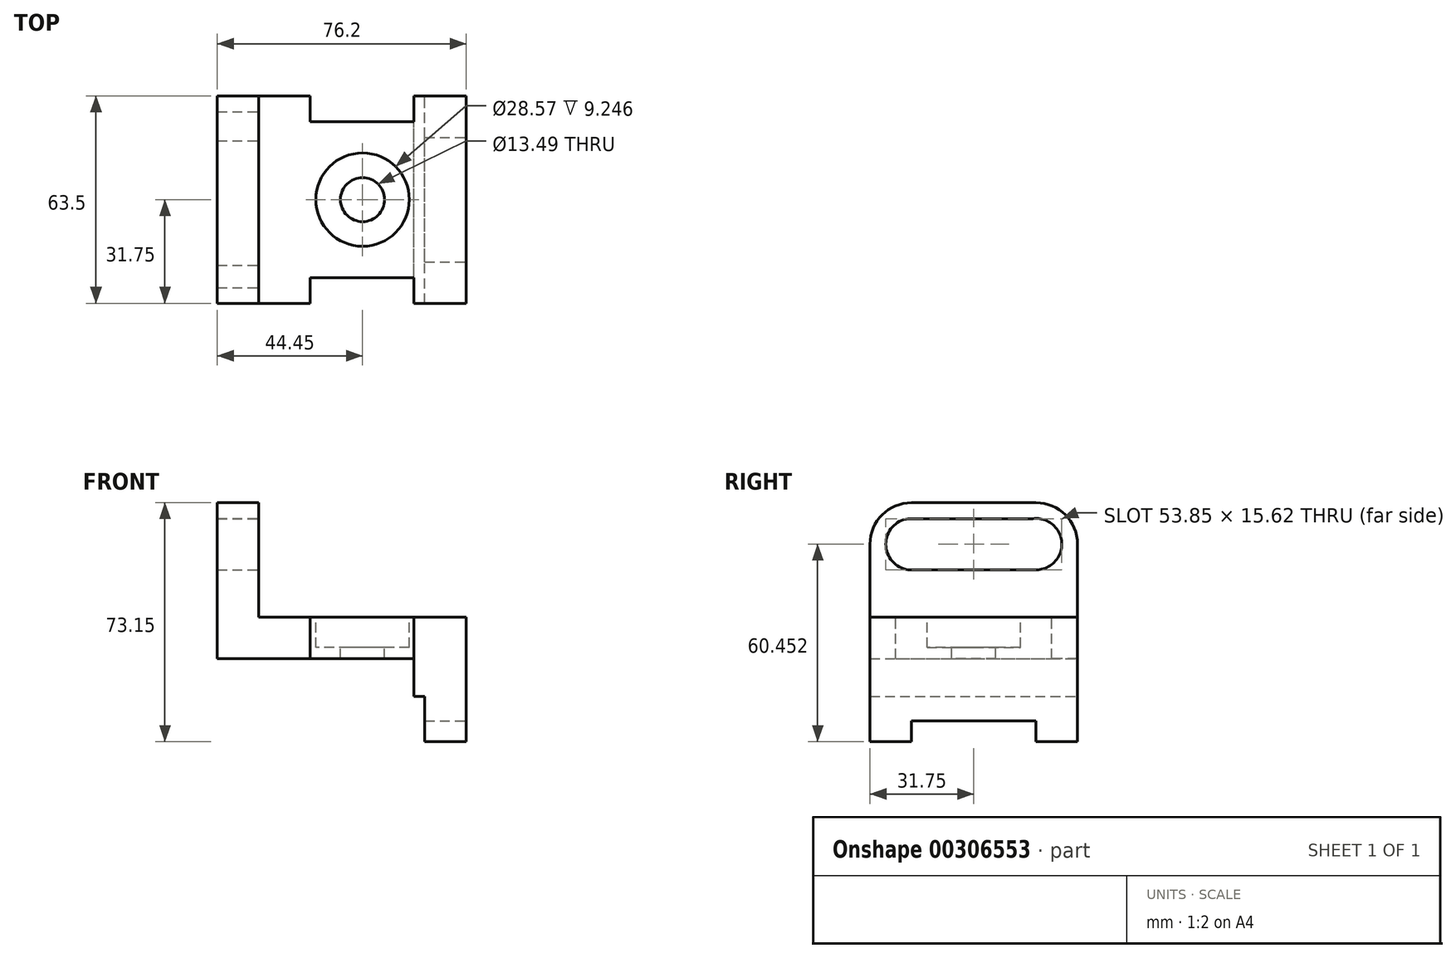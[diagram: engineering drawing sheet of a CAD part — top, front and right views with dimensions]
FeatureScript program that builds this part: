
annotation { "Feature Type Name" : "Feature", "Feature Type Description" : "" }
export const myFeature = defineFeature(function(context is Context, id is Id, definition is map)
    precondition{}
    {
        {
            var Q0;
            Q0=qCreatedBy(makeId("Front.planeOp"),FACE);
            var sketch = newSketch(context, id + "F0", { "sketchPlane" : qUnion([Q0])});
            skLineSegment(sketch, "E0", {"start": v(0, 0) * mm, "end": v(47.5, 0) * mm});
            skLineSegment(sketch, "E1", {"start": v(47.5, 0) * mm, "end": v(47.5, -11.58) * mm});
            skLineSegment(sketch, "E2", {"start": v(47.5, -11.58) * mm, "end": v(50.8, -11.58) * mm});
            skLineSegment(sketch, "E3", {"start": v(50.8, -11.58) * mm, "end": v(50.8, -25.4) * mm});
            skLineSegment(sketch, "E4", {"start": v(50.8, -25.4) * mm, "end": v(63.5, -25.4) * mm});
            skLineSegment(sketch, "E5", {"start": v(63.5, -25.4) * mm, "end": v(63.5, 12.7) * mm});
            skLineSegment(sketch, "E6", {"start": v(63.5, 12.7) * mm, "end": v(0, 12.7) * mm});
            skLineSegment(sketch, "E7", {"start": v(0, 12.7) * mm, "end": v(0, 0) * mm});
            skLineSegment(sketch, "E8", {"start": v(47.5, -11.58) * mm, "end": v(47.5, 0) * mm});
            skLineSegment(sketch, "E9", {"start": v(47.5, 12.7) * mm, "end": v(63.5, 12.7) * mm});
            skPoint(sketch, "E10.start.orphan", {"position": v(7.87, 0) * mm});
            skSolve(sketch);
        }
        {
            var Q0;
            Q0=makeQuery(id+"F0.imprint","IMPRINT",FACE,{"disambiguationData":[TD([[makeQuery(id+"F0.imprint","IMPRINT",EDGE,{"derivedFrom":sQuery(id+"F0.wireOp",EDGE,"E0")}),1.0]])]});
            extrude(context, id + "F1", {"entities" : qUnion([Q0]), "depth" : 63.5 * mm});
        }
        {
            var Q0;
            Q0=makeQuery(id+"F1.opExtrude","SWEPT_FACE",FACE,{"disambiguationData":[OSD([sQuery(id+"F0.wireOp",EDGE,"E5")])]});
            var sketch = newSketch(context, id + "F2", { "sketchPlane" : qUnion([Q0])});
            skLineSegment(sketch, "E11", {"start": v(-50.8, -25.4) * mm, "end": v(-50.8, -19.05) * mm});
            skLineSegment(sketch, "E12", {"start": v(-50.8, -19.05) * mm, "end": v(-12.7, -19.05) * mm});
            skLineSegment(sketch, "E13", {"start": v(-12.7, -19.05) * mm, "end": v(-12.7, -25.4) * mm});
            skLineSegment(sketch, "E14", {"start": v(-50.8, -25.4) * mm, "end": v(-63.5, -25.4) * mm});
            skLineSegment(sketch, "E15", {"start": v(-63.5, -25.4) * mm, "end": v(-63.5, 12.7) * mm});
            skLineSegment(sketch, "E16", {"start": v(-63.5, 12.7) * mm, "end": v(0, 12.7) * mm});
            skLineSegment(sketch, "E17", {"start": v(0, 12.7) * mm, "end": v(0, -25.4) * mm});
            skLineSegment(sketch, "E18", {"start": v(0, -25.4) * mm, "end": v(-12.7, -25.4) * mm});
            skLineSegment(sketch, "E19", {"start": v(-63.5, -25.4) * mm, "end": v(0, -25.4) * mm});
            skSolve(sketch);
        }
        {
            var Q0;
            {var subQ0=sQuery(id+"F2.wireOp",EDGE,"E11");Q0=makeQuery(id+"F2.imprint","IMPRINT",FACE,{"disambiguationData":[TD([[makeQuery(id+"F2.imprint","IMPRINT",EDGE,{"derivedFrom":subQ0}),-1.0]])]});}
            extrude(context, id + "F3", {"entities" : qUnion([Q0]), "operationType" : NewBodyOperationType.REMOVE, "endBound" : BoundingType.THROUGH_ALL, "oppositeDirection" : true, "depth" : 25.4 * mm});
        }
        {
            var Q0;
            Q0=makeQuery(id+"F1.opExtrude","SWEPT_FACE",FACE,{"disambiguationData":[OSD([sQuery(id+"F0.wireOp",EDGE,"E6"),sQuery(id+"F0.wireOp",EDGE,"E9")])]});
            var sketch = newSketch(context, id + "F4", { "sketchPlane" : qUnion([Q0])});
            skLineSegment(sketch, "E20", {"start": v(15.75, -63.5) * mm, "end": v(15.75, -55.63) * mm});
            skLineSegment(sketch, "E21", {"start": v(15.75, -55.63) * mm, "end": v(47.5, -55.63) * mm});
            skLineSegment(sketch, "E22", {"start": v(47.5, -55.63) * mm, "end": v(47.5, -63.5) * mm});
            skLineSegment(sketch, "E23", {"start": v(15.75, 0) * mm, "end": v(15.75, -7.87) * mm});
            skLineSegment(sketch, "E24", {"start": v(15.75, -7.87) * mm, "end": v(47.5, -7.87) * mm});
            skLineSegment(sketch, "E25", {"start": v(47.5, -7.87) * mm, "end": v(47.5, 0) * mm});
            skLineSegment(sketch, "E26", {"start": v(47.5, 0) * mm, "end": v(15.75, 0) * mm});
            skLineSegment(sketch, "E27", {"start": v(15.75, -63.5) * mm, "end": v(47.5, -63.5) * mm});
            skCircle(sketch, "E28", {"center": v(31.75, -31.75) * mm, "radius": 14.29 * mm});
            skCircle(sketch, "E29", {"center": v(31.75, -31.75) * mm, "radius": 6.74 * mm});
            skSolve(sketch);
        }
        {
            var Q0;
            Q0=makeQuery(id+"F4.imprint","IMPRINT",FACE,{"disambiguationData":[TD([[makeQuery(id+"F4.imprint","IMPRINT",EDGE,{"derivedFrom":sQuery(id+"F4.wireOp",EDGE,"E23")}),1.0]])]});
            var Q1;
            Q1=makeQuery(id+"F4.imprint","IMPRINT",FACE,{"disambiguationData":[TD([[makeQuery(id+"F4.imprint","IMPRINT",EDGE,{"derivedFrom":sQuery(id+"F4.wireOp",EDGE,"E20")}),-1.0]])]});
            extrude(context, id + "F5", {"entities" : qUnion([Q0, Q1]), "operationType" : NewBodyOperationType.REMOVE, "endBound" : BoundingType.THROUGH_ALL, "oppositeDirection" : true, "depth" : 25.4 * mm});
        }
        {
            var Q0;
            Q0=makeQuery(id+"F4.imprint","IMPRINT",FACE,{"disambiguationData":[TD([[makeQuery(id+"F4.imprint","IMPRINT",EDGE,{"derivedFrom":sQuery(id+"F4.wireOp",EDGE,"E28")}),1.0]])]});
            extrude(context, id + "F6", {"entities" : qUnion([Q0]), "operationType" : NewBodyOperationType.REMOVE, "oppositeDirection" : true, "depth" : 9.25 * mm});
        }
        {
            var Q0;
            Q0=makeQuery(id+"F4.imprint","IMPRINT",FACE,{"disambiguationData":[TD([[makeQuery(id+"F4.imprint","IMPRINT",EDGE,{"derivedFrom":sQuery(id+"F4.wireOp",EDGE,"E29")}),1.0]])]});
            extrude(context, id + "F7", {"entities" : qUnion([Q0]), "operationType" : NewBodyOperationType.REMOVE, "endBound" : BoundingType.THROUGH_ALL, "oppositeDirection" : true, "depth" : 25.4 * mm});
        }
        {
            var Q0;
            Q0=makeQuery(id+"F1.opExtrude","SWEPT_FACE",FACE,{"disambiguationData":[OSD([sQuery(id+"F0.wireOp",EDGE,"E7")])]});
            var sketch = newSketch(context, id + "F8", { "sketchPlane" : qUnion([Q0])});
            skLineSegment(sketch, "E30", {"start": v(0, 12.7) * mm, "end": v(0, 35.05) * mm});
            skLineSegment(sketch, "E31", {"start": v(63.5, 12.7) * mm, "end": v(63.5, 35.05) * mm});
            skLineSegment(sketch, "E32", {"start": v(0, 35.05) * mm, "end": v(63.5, 35.05) * mm, "construction": true});
            skPoint(sketch, "E33.endSnap0", {"position": v(31.75, 35.05) * mm});
            skLineSegment(sketch, "E34", {"start": v(31.75, 12.7) * mm, "end": v(31.75, 51.6) * mm, "construction": true});
            skArc(sketch, "E35", {"start": v(51.8, 42.86) * mm, "mid": v(58.67, 35.05) * mm, "end": v(51.8, 27.24) * mm});
            skArc(sketch, "E36", {"start": v(13.7, 42.86) * mm, "mid": v(4.83, 35.05) * mm, "end": v(13.7, 27.24) * mm});
            skLineSegment(sketch, "E37", {"start": v(13.7, 42.86) * mm, "end": v(51.8, 42.86) * mm});
            skLineSegment(sketch, "E38", {"start": v(51.8, 27.24) * mm, "end": v(13.7, 27.24) * mm});
            skArc(sketch, "E39", {"start": v(0, 35.05) * mm, "mid": v(3.72, 44.03) * mm, "end": v(12.7, 47.75) * mm});
            skLineSegment(sketch, "E40", {"start": v(12.7, 47.75) * mm, "end": v(50.8, 47.75) * mm});
            skArc(sketch, "E41", {"start": v(50.8, 47.75) * mm, "mid": v(59.78, 44.03) * mm, "end": v(63.5, 35.05) * mm});
            skLineSegment(sketch, "E42", {"start": v(0, 12.7) * mm, "end": v(0, 0) * mm});
            skLineSegment(sketch, "E43", {"start": v(0, 0) * mm, "end": v(63.5, 0) * mm});
            skLineSegment(sketch, "E44", {"start": v(63.5, 0) * mm, "end": v(63.5, 12.7) * mm});
            skSolve(sketch);
        }
        {
            var Q0;
            Q0=makeQuery(id+"F8.imprint","IMPRINT",FACE,{"disambiguationData":[TD([[makeQuery(id+"F8.imprint","IMPRINT",EDGE,{"derivedFrom":sQuery(id+"F8.wireOp",EDGE,"E30")}),-1.0]])]});
            var Q1;
            Q1=makeQuery(id+"F8.imprint","IMPRINT",FACE,{"disambiguationData":[TD([[makeQuery(id+"F8.imprint","IMPRINT",EDGE,{"derivedFrom":sQuery(id+"F8.wireOp",EDGE,"E42")}),1.0]])]});
            extrude(context, id + "F9", {"entities" : qUnion([Q0, Q1]), "operationType" : NewBodyOperationType.ADD, "depth" : 12.7 * mm});
        }
    });
